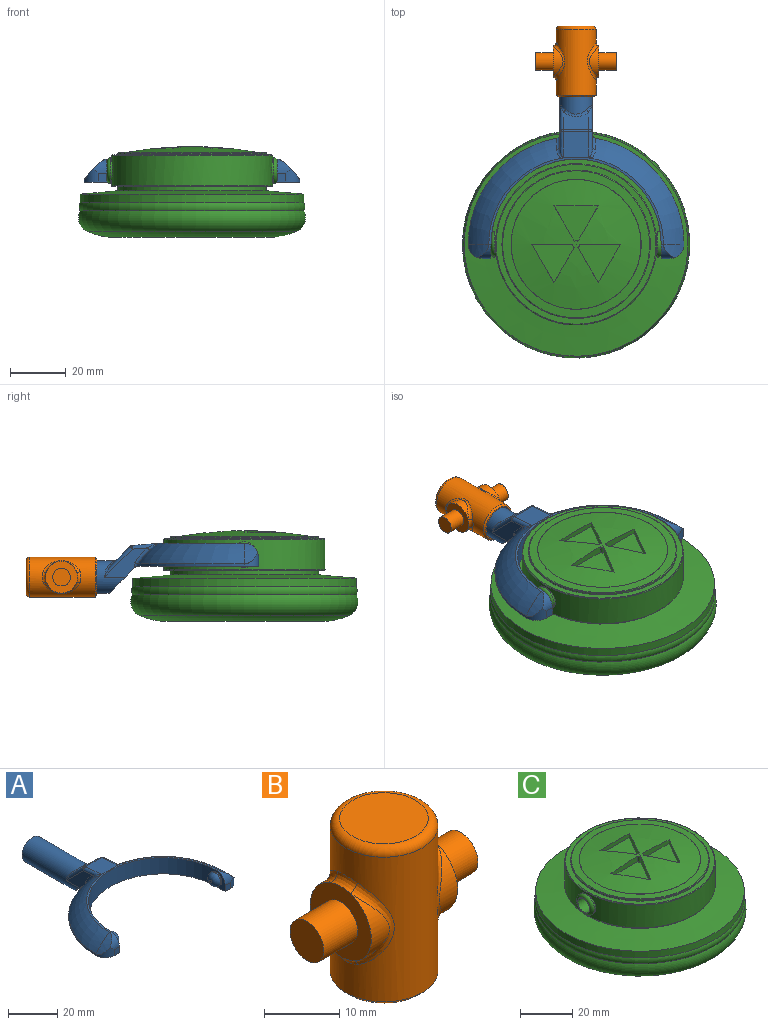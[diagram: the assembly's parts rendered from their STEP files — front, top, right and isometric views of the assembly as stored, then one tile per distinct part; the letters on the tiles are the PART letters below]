
ASSEMBLY  parts=3 mates=2
PART A: 48 faces, bbox 77.3x80.8x18.2 mm
  f0: plane 11.99x9.83mm, normal (0,-0.71,-0.71), area 141.5mm2, adj f1,f2,f9,f30,f43,f46
  f1: plane 15.39x10.49mm, normal (-1,0,0), area 63.5mm2, adj f0,f30,f32,f36,f46,f47
  f2: plane 15.39x10.49mm, normal (1,0,0), area 63.5mm2, adj f0,f30,f34,f39,f43,f44
  f3: plane 9.14x6.37mm, normal (0,0.71,0.71), area 67.6mm2, adj f35,f36,f39,f40
  f4: cylinder r=38.61mm len=37.99mm, axis (0,0,-1), area 42.6mm2, adj f6,f9,f17,f46,f47
  f5: torus R=19.3mm, axis (0,0,-1), area 507.8mm2, adj f10,f11,f12,f29,f42,f44
  f6: torus R=19.3mm, axis (0,0,-1), area 507.8mm2, adj f4,f11,f15,f28,f45,f47
  f7: cylinder r=30.48mm len=60.96mm, axis (0,0,-1), area 746.6mm2, adj f8,f9,f11,f14,f21,f24
  f8: plane 8.13x5.08mm, normal (-1,0,0), area 19.9mm2, adj f7,f9,f13,f19,f24
  f9: plane 77.22x43.73mm, normal (0,0,-1), area 956.2mm2, adj f0,f4,f7,f8,f10,f13,f14,f16
  f10: cylinder r=38.61mm len=37.99mm, axis (0,0,-1), area 42.6mm2, adj f5,f9,f20,f43,f44
  f11: plane 62.55x30.95mm, normal (0,0,1), area 75mm2, adj f5,f6,f7,f18,f19,f27
  f12: cylinder r=22.71mm len=7.33mm, axis (0,1,0), area 24.8mm2, adj f5,f19,f20
  f13: plane 3.05x3.05mm, normal (0,-1,0), area 9.3mm2, adj f8,f9,f19,f20
  f14: plane 8.13x5.08mm, normal (1,0,0), area 19.9mm2, adj f7,f9,f16,f18,f21
  f15: cylinder r=22.71mm len=7.33mm, axis (0,1,0), area 24.8mm2, adj f6,f17,f18
  f16: plane 3.05x3.05mm, normal (0,-1,0), area 9.3mm2, adj f9,f14,f17,f18
  f17: cylinder r=5.08mm len=5.08mm, axis (0,0,-1), area 21.9mm2, adj f4,f9,f15,f16,f18
  f18: cylinder r=5.08mm len=5.08mm, axis (-1,0,0), area 21.9mm2, adj f11,f14,f15,f16,f17
  f19: cylinder r=5.08mm len=5.08mm, axis (-1,0,0), area 21.9mm2, adj f8,f11,f12,f13,f20
  f20: cylinder r=5.08mm len=5.08mm, axis (0,0,-1), area 21.9mm2, adj f9,f10,f12,f13,f19
  f21: cylinder r=3.17mm len=6.35mm, axis (-1,0,0), area 12.7mm2, adj f7,f14,f23
  f22: plane 1.27x1.27mm, normal (1,0,0), area 1.3mm2, adj f23
  f23: torus R=0.64mm, axis (1,0,0), area 56.5mm2, adj f21,f22
  f24: cylinder r=3.17mm len=6.35mm, axis (1,0,0), area 12.7mm2, adj f7,f8,f26
  f25: plane 1.27x1.27mm, normal (-1,0,0), area 1.3mm2, adj f26
  f26: torus R=0.64mm, axis (-1,0,0), area 56.5mm2, adj f24,f25
  f27: plane 9.86x9.36mm, normal (0,0.09,1), area 85.6mm2, adj f11,f28,f29,f32,f34,f35,f42,f45
  f28: plane 1.04x0.17mm, normal (0,-1,0), area 0mm2, adj f6,f27,f45
  f29: plane 1.04x0.17mm, normal (0,-1,0), area 0mm2, adj f5,f27,f42
  f30: cylinder r=5.84mm len=33.01mm, axis (0,-1,0), area 1029.7mm2, adj f0,f1,f2,f31,f38,f40,f41
  f31: plane 11.68x11.68mm, normal (0,1,0), area 107.2mm2, adj f30
  f32: cylinder r=1.27mm len=9.13mm, axis (0,-1,0.09), area 14.4mm2, adj f1,f27,f33,f45
  f33: sphere r=1.27mm, area 1.5mm2, adj f32,f35,f36
  f34: cylinder r=1.27mm len=9.13mm, axis (0,1,-0.09), area 14.4mm2, adj f2,f27,f37,f42
  f35: cylinder r=1.27mm len=9.14mm, axis (-1,0,0), area 8.1mm2, adj f3,f27,f33,f37
  f36: cylinder r=1.27mm len=10.91mm, axis (0,-0.71,0.71), area 23.1mm2, adj f1,f3,f33,f38
  f37: sphere r=1.27mm, area 1.5mm2, adj f34,f35,f39
  f38: bspline ~4.55x2.75mm, area 2.3mm2, adj f30,f36,f40
  f39: cylinder r=1.27mm len=10.91mm, axis (0,0.71,-0.71), area 23.1mm2, adj f2,f3,f37,f41
  f40: bspline ~9.14x2.56mm, area 10.7mm2, adj f3,f30,f38,f41
  f41: bspline ~5.23x3.53mm, area 2.3mm2, adj f30,f39,f40
  f42: bspline ~4.62x3.14mm, area 5.2mm2, adj f5,f27,f29,f34,f44
  f43: cylinder r=1.27mm len=1.74mm, axis (0,0,-1), area 1.9mm2, adj f0,f2,f9,f10,f44
  f44: bspline ~8.6x7.86mm, area 11.9mm2, adj f2,f5,f10,f42,f43
  f45: bspline ~4.62x3.14mm, area 5.2mm2, adj f6,f27,f28,f32,f47
  f46: cylinder r=1.27mm len=1.74mm, axis (0,0,-1), area 1.9mm2, adj f0,f1,f4,f9,f47
  f47: bspline ~8.6x7.86mm, area 11.9mm2, adj f1,f4,f6,f45,f46
PART B: 25 faces, bbox 28.9x15.5x25.4 mm
  f0: cylinder r=5.71mm len=10.81mm, axis (-1,0,0), area 26.2mm2, adj f5,f15
  f1: cylinder r=5.71mm len=10.81mm, axis (-1,0,0), area 26.2mm2, adj f8,f11
  f2: cylinder r=7.14mm len=23.5mm, axis (0,0,-1), area 763.2mm2, adj f9,f10,f11,f12,f13,f14,f15,f16
  f3: plane 11.75x11.75mm, normal (0,0,1), area 108.4mm2, adj f17
  f4: plane 13.02x13.02mm, normal (0,0,-1), area 16.3mm2, adj f22,f24
  f5: plane 11.46x11.46mm, normal (1,0,0), area 70.9mm2, adj f0,f6,f13,f16,f18
  f6: cylinder r=5.71mm len=10.81mm, axis (-1,0,0), area 26.2mm2, adj f5,f14
  f7: cylinder r=5.71mm len=10.81mm, axis (-1,0,0), area 26.2mm2, adj f8,f10
  f8: plane 11.46x11.46mm, normal (-1,0,0), area 70.9mm2, adj f1,f7,f9,f12,f20
  f9: bspline ~4.64x1.73mm, area 6.5mm2, adj f2,f8,f10,f11
  f10: bspline ~13.62x4.91mm, area 20.7mm2, adj f2,f7,f9,f12
  f11: bspline ~13.6x4.87mm, area 20.7mm2, adj f1,f2,f9,f12
  f12: bspline ~4.64x1.73mm, area 6.5mm2, adj f2,f8,f10,f11
  f13: bspline ~4.64x1.73mm, area 6.5mm2, adj f2,f5,f14,f15
  f14: bspline ~13.62x4.91mm, area 20.7mm2, adj f2,f6,f13,f16
  f15: bspline ~13.6x4.87mm, area 20.7mm2, adj f0,f2,f13,f16
  f16: bspline ~4.64x1.73mm, area 6.5mm2, adj f2,f5,f14,f15
  f17: torus R=5.87mm, axis (0,0,1), area 83.8mm2, adj f2,f3
  f18: cylinder r=3.17mm len=6.35mm, axis (-1,0,0), area 126.7mm2, adj f5,f19
  f19: plane 6.35x6.35mm, normal (1,0,0), area 31.7mm2, adj f18
  f20: cylinder r=3.17mm len=6.35mm, axis (1,0,0), area 126.7mm2, adj f8,f21
  f21: plane 6.35x6.35mm, normal (-1,0,0), area 31.7mm2, adj f20
  f22: cylinder r=6.1mm len=22.86mm, axis (0,0,-1), area 875.6mm2, adj f4,f23
  f23: plane 12.19x12.19mm, normal (0,0,-1), area 116.7mm2, adj f22
  f24: cone r=7.14mm half-angle=45deg, axis (0,0,1), area 38.5mm2, adj f2,f4
PART C: 40 faces, bbox 96.2x96.2x32.5 mm
  f0: cylinder r=28.87mm len=57.73mm, axis (0,0,-1), area 1814.4mm2, adj f30,f31,f36,f37
  f1: sphere r=135.39mm, area 1385.3mm2, adj f14,f15,f16,f17,f19,f20,f21,f22
  f2: plane 39.33x39.33mm, normal (0,0,-1), area 1214.6mm2, adj f3
  f3: torus R=20.12mm, axis (0,0,-1), area 1429.3mm2, adj f2,f4
  f4: torus R=27.74mm, axis (0,0,-1), area 3542.1mm2, adj f3,f5
  f5: torus R=35.36mm, axis (0,0,-1), area 2180.1mm2, adj f4,f6
  f6: torus R=37.35mm, axis (0,0,-1), area 734.6mm2, adj f5,f7
  f7: cylinder r=40.06mm len=80.11mm, axis (0,0,-1), area 799.1mm2, adj f6,f8
  f8: cone r=26.57mm half-angle=85deg, axis (0,0,-1), area 2833.8mm2, adj f7,f9
  f9: cylinder r=26.57mm len=53.14mm, axis (0,0,-1), area 265mm2, adj f8,f10
  f10: plane 57.23x57.23mm, normal (0,0,-1), area 354.5mm2, adj f9,f36
  f11: plane 57.23x57.23mm, normal (0,0,1), area 354.5mm2, adj f12,f37
  f12: cylinder r=26.57mm len=53.14mm, axis (0,0,-1), area 92.3mm2, adj f11,f38
  f13: cone r=26.57mm half-angle=87deg, axis (0,0,-1), area 475.4mm2, adj f38,f39
  f14: plane 14.61x2.53mm, normal (0,-1,0), area 32.2mm2, adj f1,f15,f17,f18
  f15: cylinder r=1.27mm len=2.53mm, axis (0,0,1), area 3.4mm2, adj f1,f14,f16,f18
  f16: plane 12.65x7.3mm, normal (0.87,0.5,0), area 32.2mm2, adj f1,f15,f17,f18
  f17: plane 13.75x7.94mm, normal (-0.87,0.5,0), area 28mm2, adj f1,f14,f16,f18
  f18: plane 15.24x13.75mm, normal (0,0,1), area 108.3mm2, adj f14,f15,f16,f17
  f19: cylinder r=1.27mm len=2.53mm, axis (0,0,1), area 3.4mm2, adj f1,f20,f22,f23
  f20: plane 14.61x2.53mm, normal (0,-1,0), area 32.2mm2, adj f1,f19,f21,f23
  f21: plane 13.75x7.94mm, normal (0.87,0.5,0), area 28mm2, adj f1,f20,f22,f23
  f22: plane 12.65x7.3mm, normal (-0.87,0.5,0), area 32.2mm2, adj f1,f19,f21,f23
  f23: plane 15.24x13.75mm, normal (0,0,1), area 108.3mm2, adj f19,f20,f21,f22
  f24: plane 15.88x1.84mm, normal (0,-1,0), area 28mm2, adj f1,f25,f27,f28
  f25: plane 12.65x7.3mm, normal (0.87,0.5,0), area 32.2mm2, adj f1,f24,f26,f28
  f26: cylinder r=1.27mm len=2.53mm, axis (0,0,1), area 3.4mm2, adj f1,f25,f27,f28
  f27: plane 12.65x7.3mm, normal (-0.87,0.5,0), area 32.2mm2, adj f1,f24,f26,f28
  f28: plane 15.88x12.65mm, normal (0,0,1), area 108.3mm2, adj f24,f25,f26,f27
  f29: plane 6.6x6.6mm, normal (1,0,0), area 2.6mm2, adj f34,f35
  f30: cylinder r=4.57mm len=9.14mm, axis (-1,0,0), area 15.1mm2, adj f0,f34
  f31: cylinder r=4.57mm len=9.14mm, axis (-1,0,0), area 15.1mm2, adj f0,f33
  f32: plane 6.6x6.6mm, normal (-1,0,0), area 2.6mm2, adj f33,f35
  f33: torus R=3.3mm, axis (1,0,0), area 51.5mm2, adj f31,f32
  f34: torus R=3.3mm, axis (1,0,0), area 51.5mm2, adj f29,f30
  f35: cylinder r=3.17mm len=60.96mm, axis (1,0,0), area 1216.1mm2, adj f29,f32
  f36: torus R=28.61mm, axis (0,0,1), area 72.1mm2, adj f0,f10
  f37: torus R=28.61mm, axis (0,0,-1), area 72.1mm2, adj f0,f11
  f38: torus R=26.31mm, axis (0,0,1), area 64.2mm2, adj f12,f13
  f39: torus R=23.29mm, axis (0,0,1), area 4.5mm2, adj f1,f13
PLACE A t=(32.34,27.52,20.85)mm
PLACE B rot(axis=(-1,0,0),90deg) t=(32.34,80.3,16.88)mm
PLACE C t=(32.34,27.52,33.52)mm
MATE revolute A.f24 <-> C.f30  axis (-1,0,0) through (62.82,27.52,24.92)mm
MATE revolute B.f2 <-> A.f30  axis (0,-1,0) through (32.34,103.16,16.88)mm
